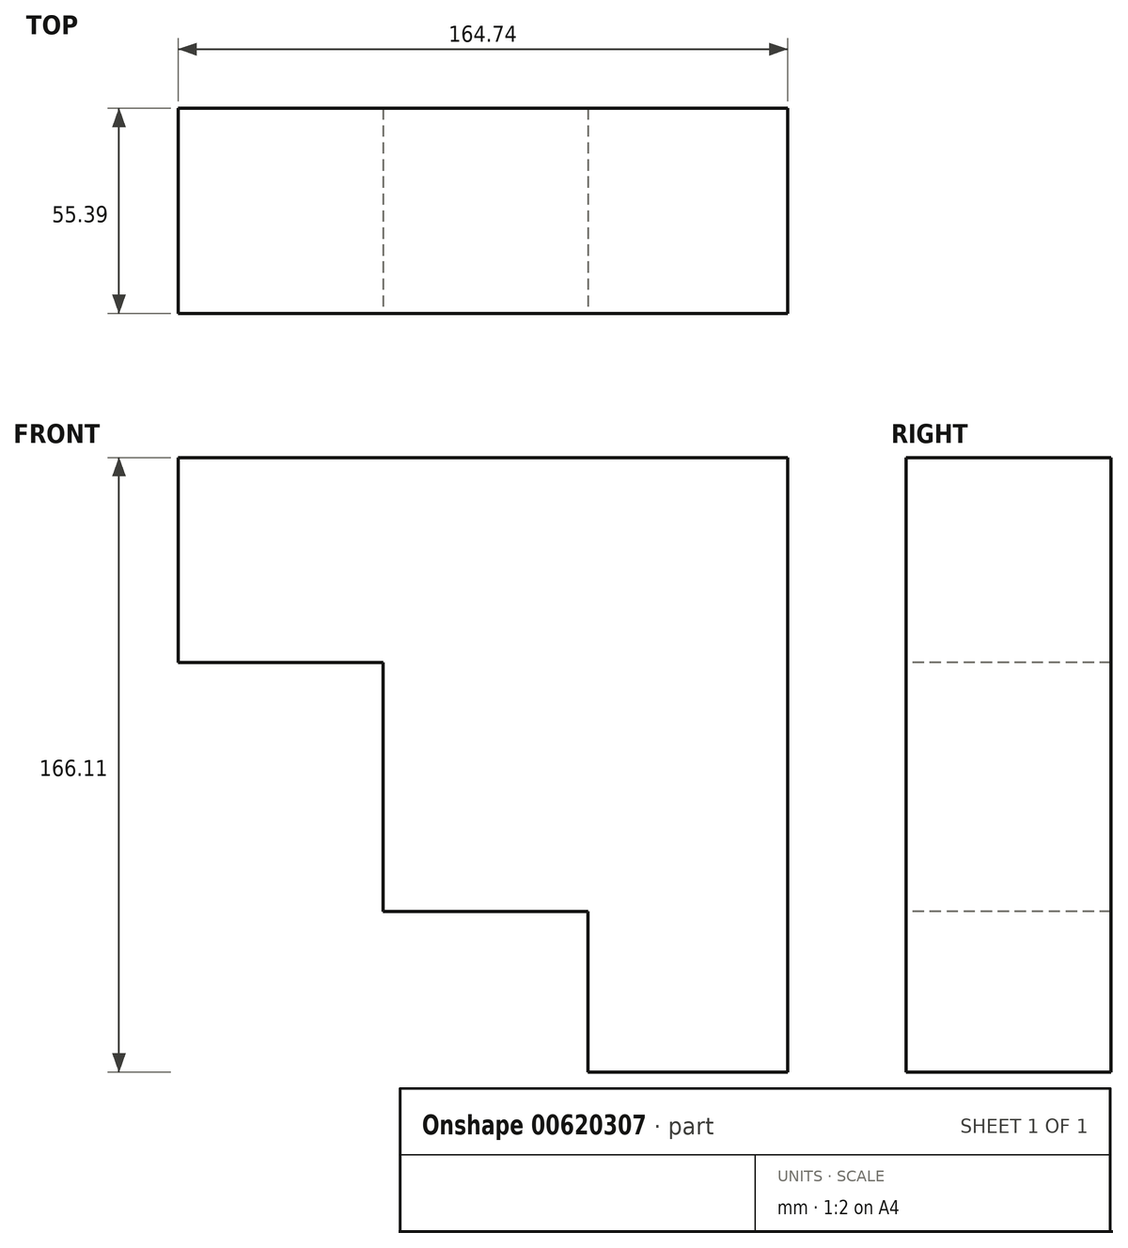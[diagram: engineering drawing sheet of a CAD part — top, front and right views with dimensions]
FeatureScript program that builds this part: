
annotation { "Feature Type Name" : "Feature", "Feature Type Description" : "" }
export const myFeature = defineFeature(function(context is Context, id is Id, definition is map)
    precondition{}
    {
        {
            var Q0;
            Q0=qCreatedBy(makeId("Top.planeOp"),FACE);
            var sketch = newSketch(context, id + "F0", { "sketchPlane" : qUnion([Q0])});
            skLineSegment(sketch, "E0.bottom", {"start": v(0, 0) * mm, "end": v(54, 0) * mm});
            skLineSegment(sketch, "E0.top", {"start": v(0, -55.4) * mm, "end": v(54, -55.4) * mm});
            skLineSegment(sketch, "E0.left", {"start": v(0, 0) * mm, "end": v(0, -55.4) * mm});
            skLineSegment(sketch, "E0.right", {"start": v(54, 0) * mm, "end": v(54, -55.4) * mm});
            skSolve(sketch);
        }
        {
            var Q0;
            Q0 = qSketchRegion(id + "F0", true);
            extrude(context, id + "F1", {"entities" : qUnion([Q0]), "depth" : 55.37 * mm, "offsetDistance" : 25.4 * mm});
        }
        {
            var Q0;
            Q0=makeQuery(id+"F1.opExtrude","SWEPT_FACE",FACE,{"disambiguationData":[OSD([sQuery(id+"F0.wireOp",EDGE,"E0.left")])]});
            var sketch = newSketch(context, id + "F2", { "sketchPlane" : qUnion([Q0])});
            skLineSegment(sketch, "E1.bottom", {"start": v(0, 0) * mm, "end": v(55.4, 0) * mm});
            skLineSegment(sketch, "E1.top", {"start": v(0, 55.37) * mm, "end": v(55.4, 55.37) * mm});
            skLineSegment(sketch, "E1.left", {"start": v(0, 0) * mm, "end": v(0, 55.37) * mm});
            skLineSegment(sketch, "E1.right", {"start": v(55.4, 0) * mm, "end": v(55.4, 55.37) * mm});
            skSolve(sketch);
        }
        {
            var Q0;
            Q0 = qSketchRegion(id + "F2", true);
            extrude(context, id + "F3", {"entities" : qUnion([Q0]), "operationType" : NewBodyOperationType.ADD, "depth" : 55.37 * mm, "offsetDistance" : 25.4 * mm});
        }
        {
            var Q0;
            Q0=makeQuery(id+"F3.opExtrude","CAP_FACE",FACE,{"disambiguationData":[OSD([sQuery(id+"F2.wireOp",EDGE,"E1.bottom"),sQuery(id+"F2.wireOp",EDGE,"E1.top"),sQuery(id+"F2.wireOp",EDGE,"E1.left"),sQuery(id+"F2.wireOp",EDGE,"E1.right")])],"isStart":false});
            var sketch = newSketch(context, id + "F4", { "sketchPlane" : qUnion([Q0])});
            skLineSegment(sketch, "E2.bottom", {"start": v(0, 0) * mm, "end": v(55.4, 0) * mm});
            skLineSegment(sketch, "E2.top", {"start": v(0, 55.37) * mm, "end": v(55.4, 55.37) * mm});
            skLineSegment(sketch, "E2.left", {"start": v(0, 0) * mm, "end": v(0, 55.37) * mm});
            skLineSegment(sketch, "E2.right", {"start": v(55.4, 0) * mm, "end": v(55.4, 55.37) * mm});
            skSolve(sketch);
        }
        {
            var Q0;
            Q0 = qSketchRegion(id + "F4", true);
            extrude(context, id + "F5", {"entities" : qUnion([Q0]), "operationType" : NewBodyOperationType.ADD, "depth" : 55.37 * mm, "offsetDistance" : 25.4 * mm});
        }
        {
            var Q0;
            Q0=makeQuery(id+"F5.boolean.opBoolean","MERGE",FACE,{"derivedFrom":[makeQuery(id+"F3.boolean.opBoolean","MERGE",FACE,{"derivedFrom":[makeQuery(id+"F1.opExtrude","CAP_FACE",FACE,{"disambiguationData":[OSD([sQuery(id+"F0.wireOp",EDGE,"E0.bottom"),sQuery(id+"F0.wireOp",EDGE,"E0.top"),sQuery(id+"F0.wireOp",EDGE,"E0.left"),sQuery(id+"F0.wireOp",EDGE,"E0.right")])],"isStart":true}),makeQuery(id+"F3.opExtrude","SWEPT_FACE",FACE,{"disambiguationData":[OSD([sQuery(id+"F2.wireOp",EDGE,"E1.bottom")])]})]}),makeQuery(id+"F5.opExtrude","SWEPT_FACE",FACE,{"disambiguationData":[OSD([sQuery(id+"F4.wireOp",EDGE,"E2.bottom")])]})]});
            var sketch = newSketch(context, id + "F6", { "sketchPlane" : qUnion([Q0])});
            skLineSegment(sketch, "E3.bottom", {"start": v(0, 0) * mm, "end": v(54, 0) * mm});
            skLineSegment(sketch, "E3.top", {"start": v(0, 55.4) * mm, "end": v(54, 55.4) * mm});
            skLineSegment(sketch, "E3.left", {"start": v(0, 0) * mm, "end": v(0, 55.4) * mm});
            skLineSegment(sketch, "E3.right", {"start": v(54, 0) * mm, "end": v(54, 55.4) * mm});
            skSolve(sketch);
        }
        {
            var Q0;
            Q0 = qSketchRegion(id + "F6", true);
            extrude(context, id + "F7", {"entities" : qUnion([Q0]), "operationType" : NewBodyOperationType.ADD, "depth" : 55.37 * mm, "offsetDistance" : 25.4 * mm});
        }
        {
            var Q0;
            Q0=makeQuery(id+"F7.opExtrude","CAP_FACE",FACE,{"disambiguationData":[OSD([sQuery(id+"F6.wireOp",EDGE,"E3.bottom"),sQuery(id+"F6.wireOp",EDGE,"E3.top"),sQuery(id+"F6.wireOp",EDGE,"E3.left"),sQuery(id+"F6.wireOp",EDGE,"E3.right")])],"isStart":false});
            var sketch = newSketch(context, id + "F8", { "sketchPlane" : qUnion([Q0])});
            skLineSegment(sketch, "E4.bottom", {"start": v(0, 55.4) * mm, "end": v(54, 55.4) * mm});
            skLineSegment(sketch, "E4.top", {"start": v(0, 0) * mm, "end": v(54, 0) * mm});
            skLineSegment(sketch, "E4.left", {"start": v(0, 55.4) * mm, "end": v(0, 0) * mm});
            skLineSegment(sketch, "E4.right", {"start": v(54, 55.4) * mm, "end": v(54, 0) * mm});
            skSolve(sketch);
        }
        {
            var Q0;
            Q0=makeQuery(id+"F8.imprint","IMPRINT",FACE,{"disambiguationData":[TD([[makeQuery(id+"F8.imprint","IMPRINT",EDGE,{"derivedFrom":sQuery(id+"F8.wireOp",EDGE,"E4.bottom")}),-1.0]])]});
            var Q1;
            Q1 = qSketchRegion(id + "F8", true);
            extrude(context, id + "F9", {"entities" : qUnion([Q0, Q1]), "operationType" : NewBodyOperationType.ADD, "depth" : 55.37 * mm, "offsetDistance" : 25.4 * mm});
        }
        {
            var Q0;
            Q0=makeQuery(id+"F9.boolean.opBoolean","MERGE",FACE,{"derivedFrom":[makeQuery(id+"F7.opExtrude","SWEPT_FACE",FACE,{"disambiguationData":[OSD([sQuery(id+"F6.wireOp",EDGE,"E3.left")])]}),makeQuery(id+"F9.opExtrude","SWEPT_FACE",FACE,{"disambiguationData":[OSD([sQuery(id+"F8.wireOp",EDGE,"E4.left")])]})]});
            var sketch = newSketch(context, id + "F10", { "sketchPlane" : qUnion([Q0])});
            skLineSegment(sketch, "E5.bottom", {"start": v(0, 0) * mm, "end": v(55.4, 0) * mm});
            skLineSegment(sketch, "E5.top", {"start": v(0, -67.38) * mm, "end": v(55.4, -67.38) * mm});
            skLineSegment(sketch, "E5.left", {"start": v(0, 0) * mm, "end": v(0, -67.38) * mm});
            skLineSegment(sketch, "E5.right", {"start": v(55.4, 0) * mm, "end": v(55.4, -67.38) * mm});
            skSolve(sketch);
        }
        {
            var Q0;
            Q0 = qSketchRegion(id + "F10", true);
            extrude(context, id + "F11", {"entities" : qUnion([Q0]), "operationType" : NewBodyOperationType.ADD, "depth" : 55.37 * mm, "offsetDistance" : 25.4 * mm});
        }
    });
